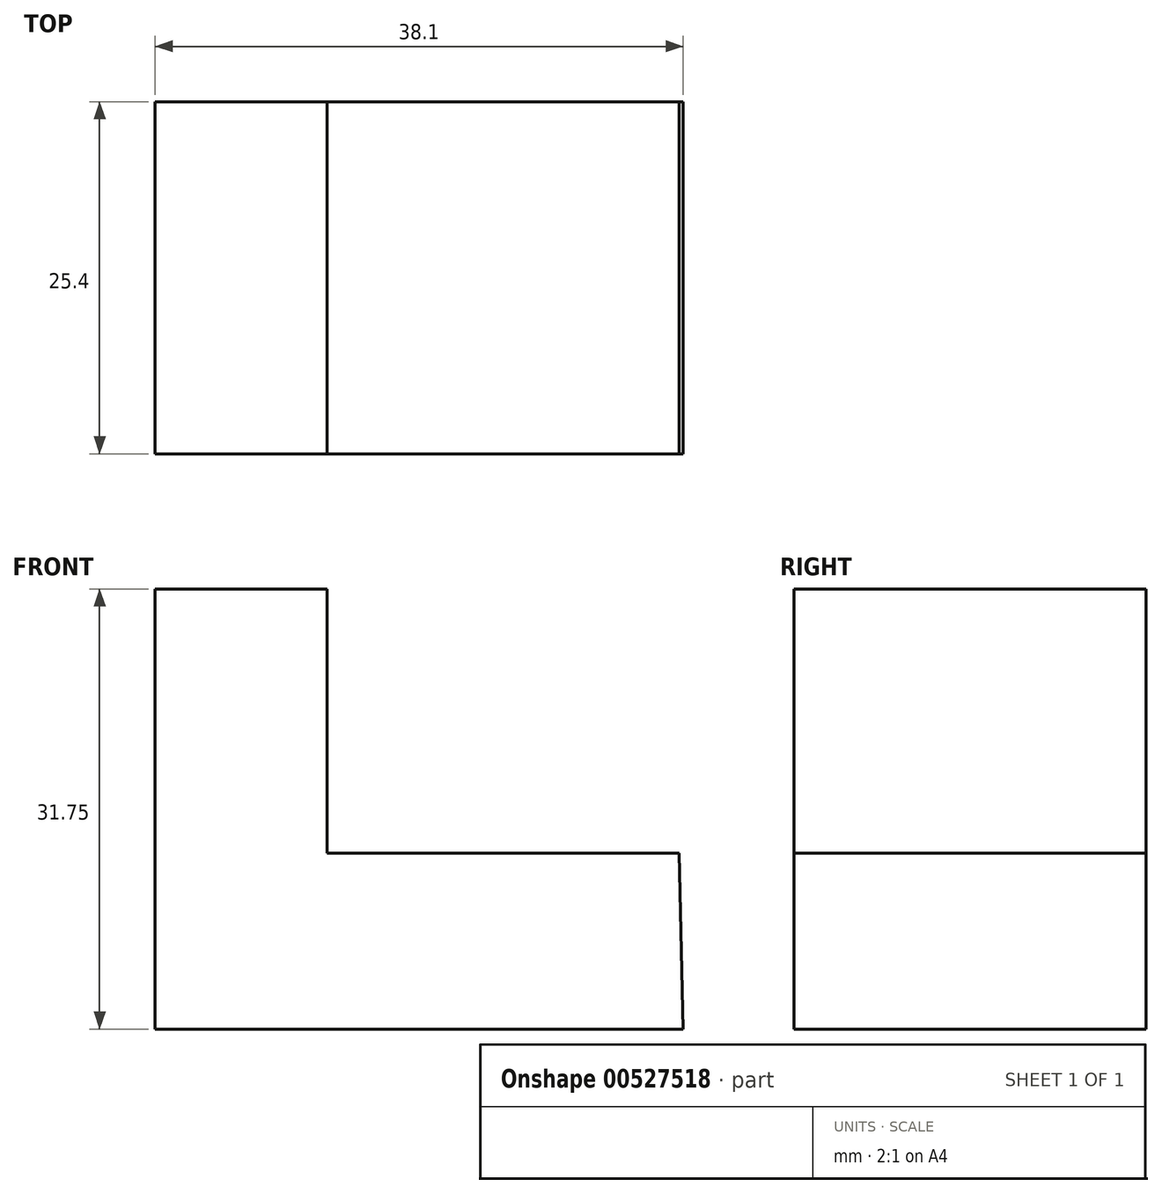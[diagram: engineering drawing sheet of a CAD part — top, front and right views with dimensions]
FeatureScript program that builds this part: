
annotation { "Feature Type Name" : "Feature", "Feature Type Description" : "" }
export const myFeature = defineFeature(function(context is Context, id is Id, definition is map)
    precondition{}
    {
        {
            var Q0;
            Q0=qCreatedBy(makeId("Front.planeOp"),FACE);
            var sketch = newSketch(context, id + "F0", { "sketchPlane" : qUnion([Q0])});
            skLineSegment(sketch, "E0", {"start": v(38.1, 0) * mm, "end": v(0, 0) * mm});
            skLineSegment(sketch, "E1", {"start": v(0, 0) * mm, "end": v(0, 31.75) * mm});
            skLineSegment(sketch, "E2", {"start": v(0, 31.75) * mm, "end": v(12.41, 31.75) * mm});
            skLineSegment(sketch, "E3", {"start": v(12.41, 31.75) * mm, "end": v(12.41, 12.7) * mm});
            skLineSegment(sketch, "E4", {"start": v(12.41, 12.7) * mm, "end": v(37.81, 12.7) * mm});
            skLineSegment(sketch, "E5", {"start": v(37.81, 12.7) * mm, "end": v(38.1, 0) * mm});
            skSolve(sketch);
        }
        {
            var Q0;
            Q0=makeQuery(id+"F0.imprint","IMPRINT",FACE,{"disambiguationData":[TD([[makeQuery(id+"F0.imprint","IMPRINT",EDGE,{"derivedFrom":sQuery(id+"F0.wireOp",EDGE,"E0")}),-1.0]])]});
            extrude(context, id + "F1", {"entities" : qUnion([Q0]), "depth" : 25.4 * mm, "offsetDistance" : 25.4 * mm});
        }
    });
